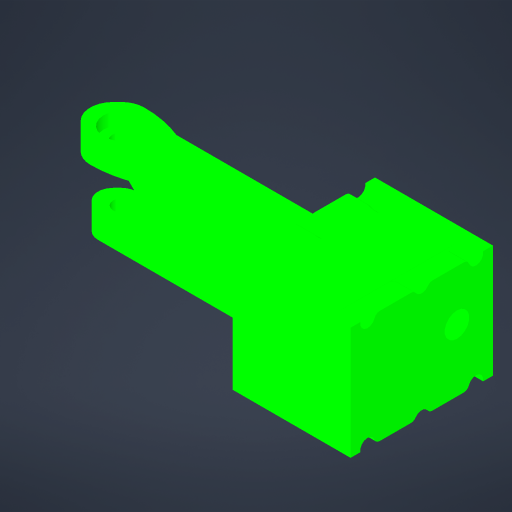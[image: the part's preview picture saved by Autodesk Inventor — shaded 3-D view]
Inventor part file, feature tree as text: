
AUTODESK INVENTOR PART (.ipt)
format: ipt  version: 2023.4 (Build 274418000, 418)  size: 592,384 bytes
history: native  units: mm
features: extrude x10, sketch x6, projected_geometry x6, chamfer x5, reference x5, fillet x3, other x3, plane x2
ambient origin geometry x8: Origin, YZ Plane, XZ Plane, XY Plane, X Axis, Y Axis, Z Axis, Center Point
bodies: Solid1 (feature_tree)
feature tree (40):
  sketch  "Sketch1"  dims[d0=0.5mm d1=19.097444mm d2=0.0mm]
  plane  "Work Plane1"
  extrude  "Extrusion1"  Depth=19.097444mm TaperAngle=0.0deg
  plane  "Work Plane2"
  extrude  "Extrusion2"  [1 undecoded]
  chamfer  "Chamfer1"  Distance=8.375mm
  extrude  "Extrusion4"  Depth=0.25mm
  chamfer  "Chamfer2"  Distance=33.75mm
  chamfer  "Chamfer3"  Distance=35.0mm
  fillet  "Fillet1"  Radius=2.5mm
  sketch  "Sketch5"  dims[d18=7.5mm d19=35.0mm d20=0.0mm]
  extrude  "Extrusion5"  Depth=0.875mm
  extrude  "Extrusion6"  Depth=0.875mm
  extrude  "Extrusion7"  Depth=0.875mm
  extrude  "Extrusion8"  Depth=0.875mm
  extrude  "Extrusion9"  Depth=0.875mm
  extrude  "Extrusion10"  Depth=0.875mm
  extrude  "Extrusion12"  Depth=10.0mm TaperAngle=0.0deg
  chamfer  "Chamfer4"  Distance=2.0mm
  chamfer  "Chamfer5"  Distance=2.0mm
  fillet  "Fillet2"  Radius=10.0mm
  fillet  "Fillet3"  Radius=2.375mm
  reference  "Reference1"
  sketch  "Sketch2"  dims[d3=4.0mm d4=-2.5mm d7=8.375mm d8=0.0mm]
  projected_geometry  "Projected Loop1"
  sketch  "Sketch3"  dims[d11=1.25mm d12=2.0mm d13=45.0deg d14=0.25mm d15=33.75mm d16=0.0mm]
  projected_geometry  "Projected Loop2"
  reference  "Reference2"
  reference  "Reference3"
  reference  "Reference4"
  reference  "Reference5"
  sketch  "Sketch4"  dims[d17=10.0mm]
  projected_geometry  "Projected Loop3"
  projected_geometry  "Projected Loop4"
  projected_geometry  "Projected Loop5"
  sketch  "Sketch6"  dims[d21=1.875mm d22=2.0mm d23=45.0deg d24=2.5mm d25=2.0mm d26=45.0deg d27=2.5mm d35=1.5mm d36=2.875mm d37=3.125mm d38=6.0mm d39=1.25mm d40=10.0mm d41=0.0mm d42=2.0mm d43=0.0mm d44=2.0mm d45=0.0mm d46=10.0mm d47=0.0mm d48=2.375mm d49=2.375mm d50=2.375mm d54=12.5mm d55=20.0mm d56=10.0mm d57=0.0mm d58=10.0mm d59=0.0mm d60=1.71875mm d61=2.0mm d62=45.0deg d63=0.875mm d64=0.25mm d65=6.0mm d66=0.875mm d67=2.5mm d68=2.5mm d69=0.0mm d70=0.0mm d71=0.0mm d72=0.0mm d73=0.0mm d74=0.0mm d75=0.0mm d76=0.0mm d77=5.0mm d78=0.0mm d79=0.5mm d80=2.0mm d81=45.0deg d51=0.872665mm d82=0.5mm d83=0.872665mm d84=0.5mm d85=0.872665mm]
  projected_geometry  "Projected Loop6"
  other  "XYZ Stage V5.iam"
  other  "Y Stage Body v5:1"
  other  "Y Stage Part V5:1"
note: 1 required parameter value undecoded (feature->parameter linkage not recoverable at this tier; creation-order binding heuristic only, values carry confidence <= 0.55)
